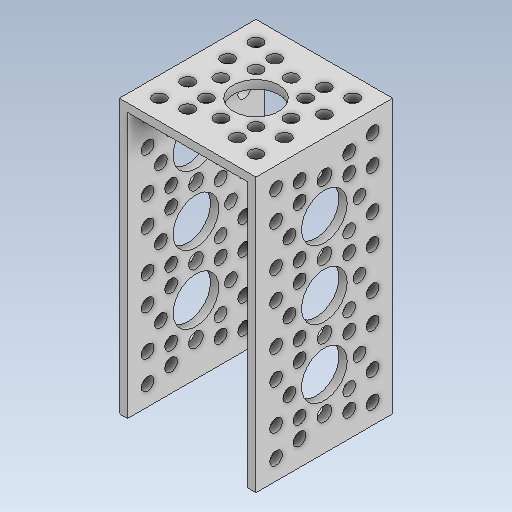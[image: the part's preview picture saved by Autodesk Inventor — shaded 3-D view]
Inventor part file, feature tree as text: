
AUTODESK INVENTOR PART (.ipt)
format: ipt  version: 2020 (Build 240168000, 168)  size: 354,816 bytes
history: native  units: in
note: dims shown in document units (in); Inventor stores cm internally (conversion verified against a paired STEP export)
features: mirror x1
ambient origin geometry x8: Origin, YZ Plane, XZ Plane, XY Plane, X Axis, Y Axis, Z Axis, Center Point
bodies: Solid1 (feature_tree)
feature tree (1):
  mirror  "Mirror4"
